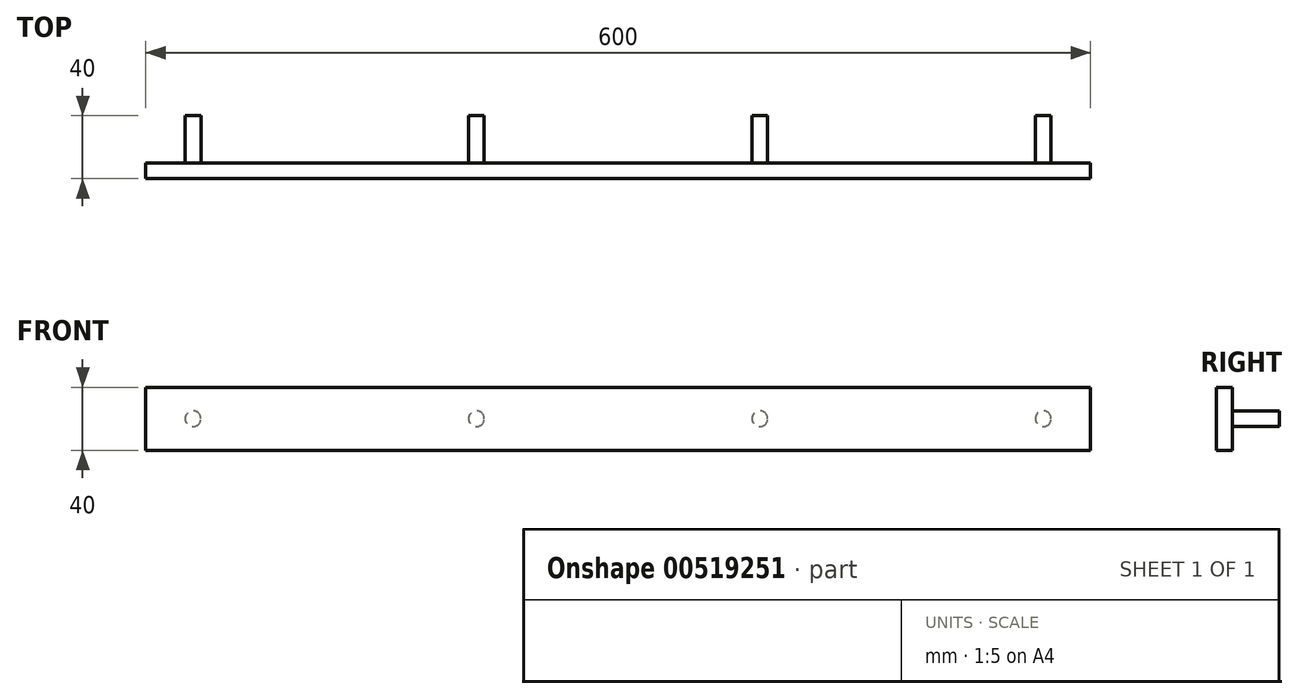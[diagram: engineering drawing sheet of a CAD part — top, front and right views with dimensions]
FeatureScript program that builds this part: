
annotation { "Feature Type Name" : "Feature", "Feature Type Description" : "" }
export const myFeature = defineFeature(function(context is Context, id is Id, definition is map)
    precondition{}
    {
        {
            var Q0;
            Q0=qCreatedBy(makeId("Right.planeOp"),FACE);
            var sketch = newSketch(context, id + "F0", { "sketchPlane" : qUnion([Q0])});
            skLineSegment(sketch, "E0.bottom", {"start": v(0, 0) * mm, "end": v(10, 0) * mm});
            skLineSegment(sketch, "E0.top", {"start": v(0, 40) * mm, "end": v(10, 40) * mm});
            skLineSegment(sketch, "E0.left", {"start": v(0, 0) * mm, "end": v(0, 40) * mm});
            skLineSegment(sketch, "E0.right", {"start": v(10, 0) * mm, "end": v(10, 40) * mm});
            skSolve(sketch);
        }
        {
            var Q0;
            Q0=qSketchRegion(id+"F0",true);
            extrude(context, id + "F1", {"entities" : qUnion([Q0]), "oppositeDirection" : true, "depth" : 600 * mm, "offsetDistance" : 25 * mm});
        }
        {
            var Q0;
            Q0=makeQuery(id+"F1.opExtrude","SWEPT_FACE",FACE,{"disambiguationData":[OSD([sQuery(id+"F0.wireOp",EDGE,"E0.right")])]});
            var sketch = newSketch(context, id + "F2", { "sketchPlane" : qUnion([Q0])});
            skCircle(sketch, "E1", {"center": v(570, 20) * mm, "radius": 5 * mm});
            skPoint(sketch, "E1.centerSnap0", {"position": v(600, 20) * mm});
            skCircle(sketch, "E2.1.0.0", {"center": v(390, 20) * mm, "radius": 5 * mm});
            skCircle(sketch, "E2.2.0.0", {"center": v(210, 20) * mm, "radius": 5 * mm});
            skCircle(sketch, "E2.3.0.0", {"center": v(30, 20) * mm, "radius": 5 * mm});
            skLineSegment(sketch, "E2.direction1", {"start": v(390, 20) * mm, "end": v(570, 20) * mm, "construction": true});
            skSolve(sketch);
        }
        {
            var Q0;
            Q0 = qSketchRegion(id + "F2", true);
            extrude(context, id + "F3", {"entities" : qUnion([Q0]), "operationType" : NewBodyOperationType.ADD, "depth" : 30 * mm, "offsetDistance" : 25 * mm});
        }
    });
